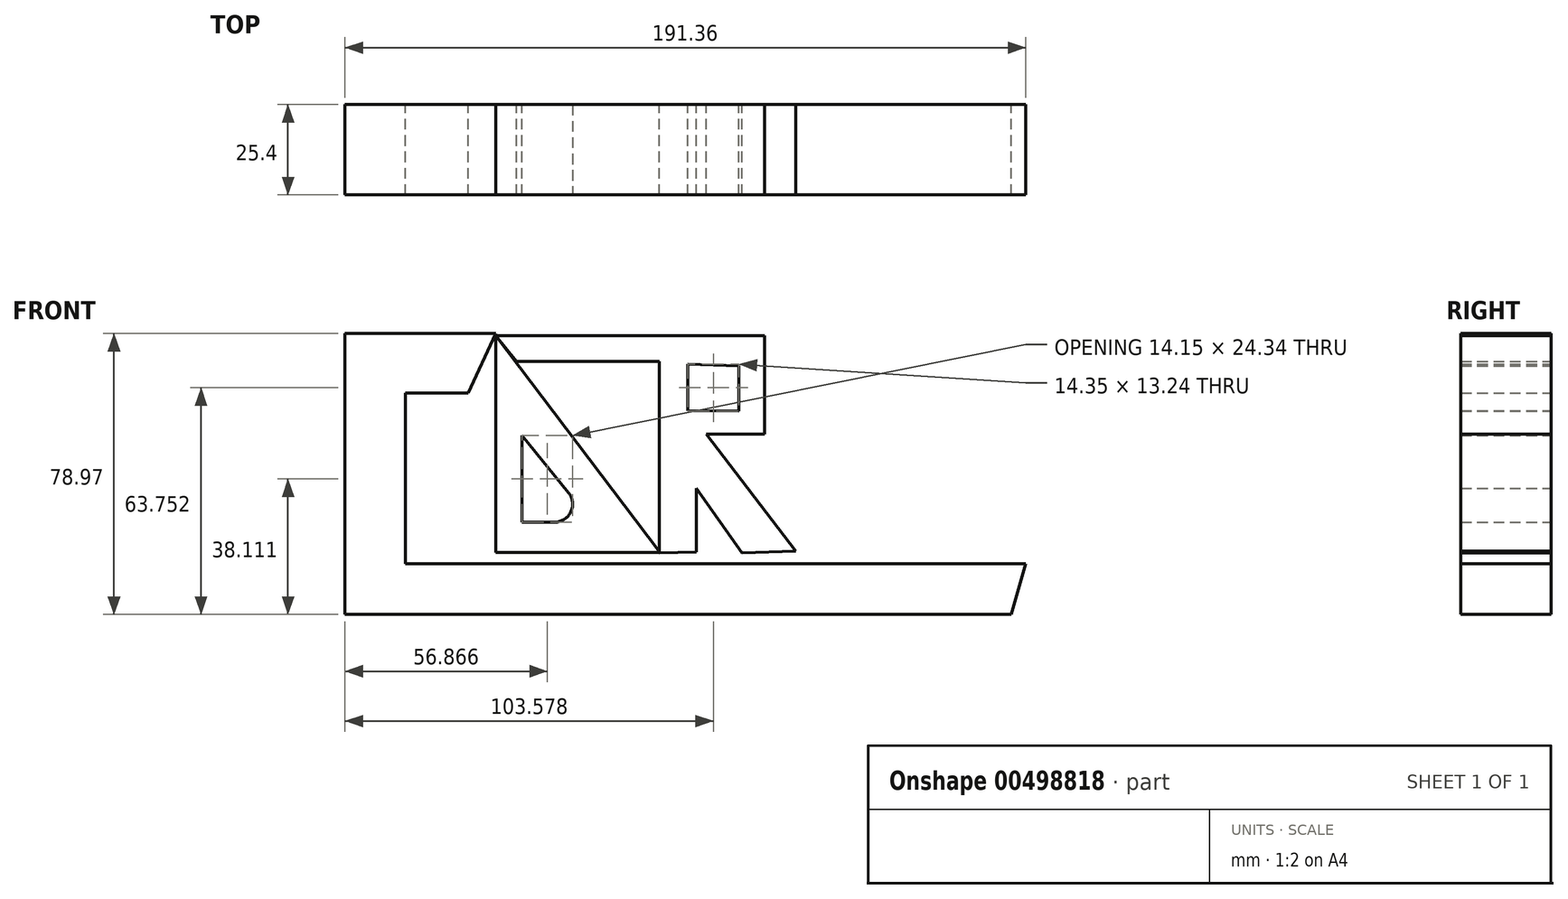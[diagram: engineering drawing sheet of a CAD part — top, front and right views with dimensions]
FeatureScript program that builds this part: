
annotation { "Feature Type Name" : "Feature", "Feature Type Description" : "" }
export const myFeature = defineFeature(function(context is Context, id is Id, definition is map)
    precondition{}
    {
        {
            var Q0;
            Q0=qCreatedBy(makeId("Front.planeOp"),FACE);
            var sketch = newSketch(context, id + "F0", { "sketchPlane" : qUnion([Q0])});
            skLineSegment(sketch, "E0", {"start": v(0, 43.55) * mm, "end": v(-28, 43.55) * mm});
            skLineSegment(sketch, "E1", {"start": v(-28, 43.55) * mm, "end": v(-42.43, 43.55) * mm});
            skLineSegment(sketch, "E2", {"start": v(-42.43, 43.55) * mm, "end": v(-42.43, -15.98) * mm});
            skLineSegment(sketch, "E3", {"start": v(-42.43, -15.98) * mm, "end": v(-42.43, -35.42) * mm});
            skLineSegment(sketch, "E4", {"start": v(-42.43, -35.42) * mm, "end": v(-8.76, -35.42) * mm});
            skLineSegment(sketch, "E5", {"start": v(-8.76, -35.42) * mm, "end": v(38.21, -35.42) * mm});
            skLineSegment(sketch, "E6", {"start": v(38.21, -35.42) * mm, "end": v(92.25, -35.42) * mm});
            skLineSegment(sketch, "E7", {"start": v(92.25, -35.42) * mm, "end": v(144.83, -35.42) * mm});
            skLineSegment(sketch, "E8", {"start": v(144.83, -35.42) * mm, "end": v(148.93, -21.11) * mm});
            skLineSegment(sketch, "E9", {"start": v(148.93, -21.11) * mm, "end": v(0, -21.11) * mm});
            skLineSegment(sketch, "E10", {"start": v(0, -21.11) * mm, "end": v(-14.71, -21.11) * mm});
            skLineSegment(sketch, "E11", {"start": v(-14.71, -21.11) * mm, "end": v(-25.39, -21.11) * mm});
            skLineSegment(sketch, "E12", {"start": v(-25.39, -21.11) * mm, "end": v(-25.39, 26.83) * mm});
            skLineSegment(sketch, "E13", {"start": v(-25.39, 26.83) * mm, "end": v(-7.8, 26.83) * mm});
            skLineSegment(sketch, "E14", {"start": v(-7.8, 26.83) * mm, "end": v(0, 43.55) * mm});
            skSolve(sketch);
        }
        {
            var Q0;
            Q0=qCreatedBy(makeId("Front.planeOp"),FACE);
            var sketch = newSketch(context, id + "F1", { "sketchPlane" : qUnion([Q0])});
            skLineSegment(sketch, "E15", {"start": v(0, 42.96) * mm, "end": v(0, -17.98) * mm});
            skLineSegment(sketch, "E16", {"start": v(0, -17.98) * mm, "end": v(46.1, -17.98) * mm});
            skLineSegment(sketch, "E17", {"start": v(46.1, -17.98) * mm, "end": v(0, 42.96) * mm});
            skLineSegment(sketch, "E18", {"start": v(7.36, 14.86) * mm, "end": v(7.36, -9.48) * mm});
            skLineSegment(sketch, "E19", {"start": v(7.36, -9.48) * mm, "end": v(27.14, -9.48) * mm});
            skLineSegment(sketch, "E20", {"start": v(27.14, -9.48) * mm, "end": v(7.36, 14.86) * mm});
            skSolve(sketch);
        }
        {
            var Q0;
            Q0=qCreatedBy(makeId("Front.planeOp"),FACE);
            var sketch = newSketch(context, id + "F2", { "sketchPlane" : qUnion([Q0])});
            skLineSegment(sketch, "E21", {"start": v(45.94, -18.13) * mm, "end": v(45.94, 31.04) * mm});
            skLineSegment(sketch, "E22", {"start": v(45.94, 31.04) * mm, "end": v(45.94, 31.04) * mm});
            skLineSegment(sketch, "E23", {"start": v(45.94, 31.04) * mm, "end": v(45.94, 35.73) * mm});
            skLineSegment(sketch, "E24", {"start": v(45.94, 35.73) * mm, "end": v(5.83, 35.73) * mm});
            skLineSegment(sketch, "E25", {"start": v(5.83, 35.73) * mm, "end": v(0, 43) * mm});
            skLineSegment(sketch, "E26", {"start": v(0, 43) * mm, "end": v(75.52, 43) * mm});
            skLineSegment(sketch, "E27", {"start": v(75.52, 43) * mm, "end": v(75.52, 19.1) * mm});
            skLineSegment(sketch, "E28", {"start": v(75.52, 19.1) * mm, "end": v(75.52, 15.25) * mm});
            skLineSegment(sketch, "E29", {"start": v(75.52, 15.25) * mm, "end": v(59.17, 15.25) * mm});
            skLineSegment(sketch, "E30", {"start": v(59.17, 15.25) * mm, "end": v(84.29, -17.64) * mm});
            skLineSegment(sketch, "E31", {"start": v(84.29, -17.64) * mm, "end": v(69.2, -18.13) * mm});
            skLineSegment(sketch, "E32", {"start": v(69.2, -18.13) * mm, "end": v(56.32, 0) * mm});
            skLineSegment(sketch, "E33", {"start": v(56.32, 0) * mm, "end": v(56.32, -17.89) * mm});
            skLineSegment(sketch, "E34", {"start": v(56.32, -17.89) * mm, "end": v(45.94, -18.13) * mm});
            skLineSegment(sketch, "E35", {"start": v(53.97, 34.95) * mm, "end": v(53.97, 21.86) * mm});
            skLineSegment(sketch, "E36", {"start": v(53.97, 21.86) * mm, "end": v(68.32, 21.71) * mm});
            skLineSegment(sketch, "E37", {"start": v(68.32, 21.71) * mm, "end": v(68.32, 34.46) * mm});
            skLineSegment(sketch, "E38", {"start": v(68.32, 34.46) * mm, "end": v(53.97, 34.95) * mm});
            skSolve(sketch);
        }
        {
            var Q0;
            Q0=makeQuery(id+"F0.imprint","IMPRINT",FACE,{"disambiguationData":[TD([[makeQuery(id+"F0.imprint","IMPRINT",EDGE,{"derivedFrom":sQuery(id+"F0.wireOp",EDGE,"E0")}),1.0]])]});
            extrude(context, id + "F3", {"entities" : qUnion([Q0]), "depth" : 25.4 * mm, "offsetDistance" : 25.4 * mm});
        }
        {
            var Q0;
            Q0=makeQuery(id+"F1.imprint","IMPRINT",FACE,{"disambiguationData":[TD([[makeQuery(id+"F1.imprint","IMPRINT",EDGE,{"derivedFrom":sQuery(id+"F1.wireOp",EDGE,"E15")}),1.0]])]});
            extrude(context, id + "F4", {"entities" : qUnion([Q0]), "depth" : 25.4 * mm, "offsetDistance" : 25.4 * mm});
        }
        {
            var Q0;
            Q0=makeQuery(id+"F2.imprint","IMPRINT",FACE,{"disambiguationData":[TD([[makeQuery(id+"F2.imprint","IMPRINT",EDGE,{"derivedFrom":sQuery(id+"F2.wireOp",EDGE,"E21")}),-1.0]])]});
            extrude(context, id + "F5", {"entities" : qUnion([Q0]), "operationType" : NewBodyOperationType.ADD, "depth" : 25.4 * mm, "offsetDistance" : 25.4 * mm});
        }
        {
            var Q0;
            Q0=makeQuery(id+"F4.opExtrude","SWEPT_EDGE",EDGE,{"disambiguationData":[OSD([sQuery(id+"F1.wireOp",EDGE,"E19"),sQuery(id+"F1.wireOp",EDGE,"E20")])]});
            fillet(context, id + "F6", {"entities" : qUnion([Q0]), "radius" : 5.08 * mm, "tangentPropagation" : true, "allowEdgeOverflow" : false});
        }
    });
